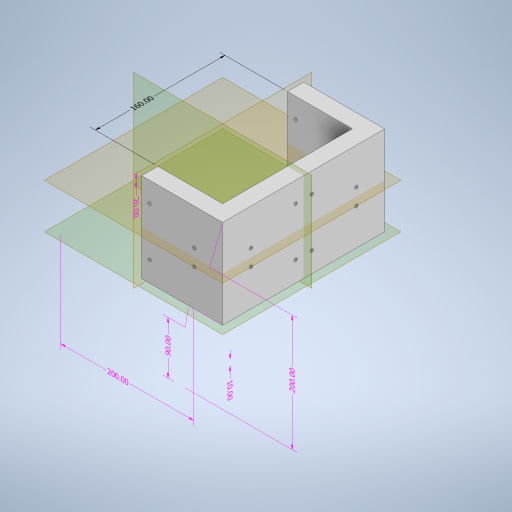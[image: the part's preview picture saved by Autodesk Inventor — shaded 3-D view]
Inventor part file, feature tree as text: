
AUTODESK INVENTOR PART (.ipt)
format: ipt  version: 2023 (Build 270158000, 158)  size: 440,832 bytes
history: native  units: mm
features: sketch x9, other x8, extrude x5, hole x4, plane x4, split x2
ambient origin geometry x8: Origin, YZ Plane, XZ Plane, XY Plane, X Axis, Y Axis, Z Axis, Center Point
bodies: Body1 (feature_tree)
feature tree (32):
  other  "Sólido1"
  other  "Anotaciones"
  extrude  "Extrusión1"  Depth=200.0mm
  hole  "Agujero1"  [1 undecoded]
  extrude  "Extrusión2"  Depth=15.0mm
  extrude  "Extrusión3"  Depth=80.0mm TaperAngle=0.0deg
  extrude  "Extrusión4"  Depth=200.0mm
  extrude  "Extrusión5"  Depth=20.0mm
  hole  "Agujero2"  [1 undecoded]
  plane  "Plano de trabajo1"
  split  "Dividir1"
  plane  "Plano de trabajo2"
  plane  "Plano de trabajo3"
  plane  "Plano de trabajo4"
  hole  "Agujero3"  [1 undecoded]
  hole  "Agujero4"  [1 undecoded]
  split  "Dividir2"
  sketch  "Boceto2"  dims[d7=15.0mm d8=200.0mm]
  sketch  "Boceto3"  dims[d9=10.0mm d10=0.0mm]
  sketch  "Boceto4"  dims[d11=3.5mm d12=1.75mm d13=1.75mm d14=1.75mm d15=1.75mm d16=10.0mm d17=10.0mm d19=40.0mm]
  sketch  "Boceto5"  dims[d20=3.5mm d21=6.0mm d22=4.0mm d23=2.0mm d24=90.0deg d25=8.0mm d26=20.594885mm d27=15.0mm]
  sketch  "Boceto6"  dims[d28=20.0mm d29=80.0mm d30=0.0mm]
  sketch  "Boceto7"  dims[d31=57.0mm d32=200.0mm]
  sketch  "Boceto8"  dims[d33=110.0mm d34=0.0mm d36=20.0mm]
  sketch  "Boceto9"  dims[d37=20.0mm d38=20.0mm]
  sketch  "Boceto10"  dims[d39=90.0mm d40=0.0mm d43=30.0mm d44=0.0mm d45=3.5mm d46=1.75mm d47=1.75mm d48=1.75mm d49=1.75mm d50=10.0mm d51=10.0mm d52=15.0mm d53=10.0mm d54=10.0mm d55=15.0mm d56=3.5mm d57=6.0mm d58=4.0mm d59=2.0mm d60=90.0deg d61=8.0mm d62=20.594885mm d63=10.0mm d65=10.0mm d75=200.0mm d76=10.0mm d77=20.0mm d81=40.0mm d88=90.0deg d89=10.0mm d90=30.0mm d91=5.0mm d92=5.0mm d93=5.0mm d94=5.0mm d95=30.0mm d96=5.0mm d97=5.0mm d98=3.5mm d99=5.0mm d100=5.0mm d101=5.0mm d102=5.0mm d103=5.0mm d104=20.0mm d105=3.5mm d106=6.0mm d107=4.0mm d108=2.0mm d109=90.0deg d110=8.0mm d111=20.594885mm d112=10.0mm d113=30.0mm d114=5.0mm d115=5.0mm d116=5.0mm d117=5.0mm d118=5.0mm d119=5.0mm d120=3.5mm d121=5.0mm d122=5.0mm d123=5.0mm d124=5.0mm d125=5.0mm d126=30.0mm d127=30.0mm d128=3.5mm d129=6.0mm d130=4.0mm d131=2.0mm d132=90.0deg d133=8.0mm d134=20.594885mm d66=5.760865mm d67=7.72461mm d68=200.0mm d69=3.008686mm d70=2.422102mm d71=10.0mm d72=3.500509mm d73=2.402572mm d74=90.0mm d78=3.13122mm d79=6.269346mm d80=200.0mm d82=8.450127mm d83=0.968417mm d84=20.0mm d85=4.759975mm d86=4.646891mm d87=160.0mm]
  other  "Cota lineal 1"
  other  "Cota lineal 2"
  other  "Cota lineal 3"
  other  "Cota lineal 4"
  other  "Cota lineal 5"
  other  "Cota lineal 6"
note: 4 required parameter values undecoded (feature->parameter linkage not recoverable at this tier; creation-order binding heuristic only, values carry confidence <= 0.55)
